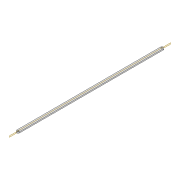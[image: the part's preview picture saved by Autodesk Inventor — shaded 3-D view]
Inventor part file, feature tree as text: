
AUTODESK INVENTOR PART (.ipt)
format: ipt  version: 2022 (Build 260153000, 153)  size: 85,504 bytes
history: native  units: mm
features: extrude x1, sketch x1
ambient origin geometry x8: Origin, YZ Plane, XZ Plane, XY Plane, X Axis, Y Axis, Z Axis, Center Point
bodies: Solid1 (feature_tree)
feature tree (2):
  extrude  "Extrusion1"  Depth=10.0mm
  sketch  "Sketch1"  dims[d0=500.0mm d1=10.0mm d2=4.0mm d3=4.0mm d4=4.0mm d5=0.0mm]
